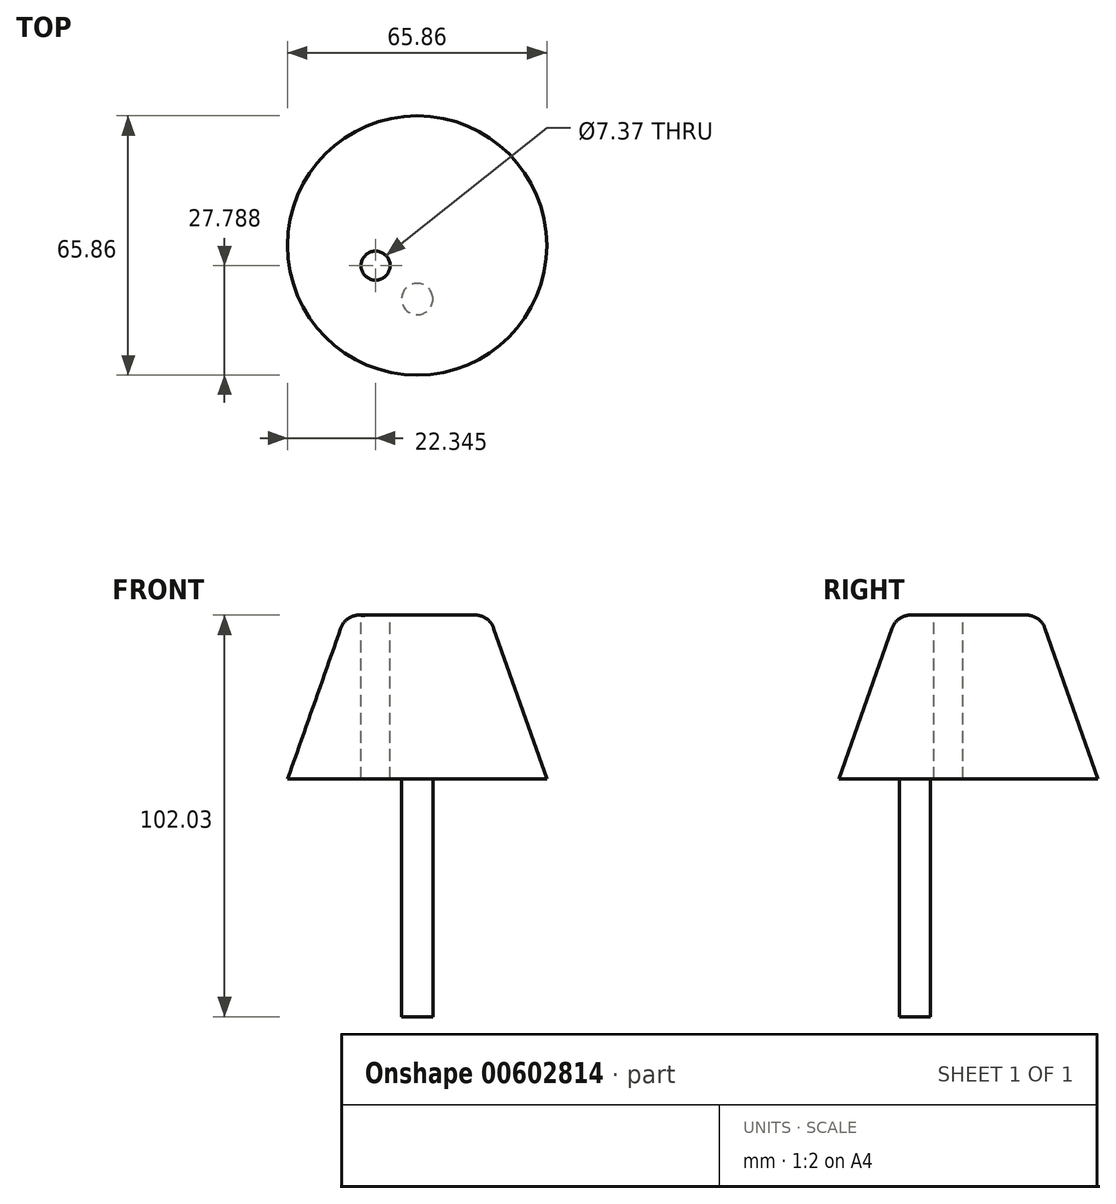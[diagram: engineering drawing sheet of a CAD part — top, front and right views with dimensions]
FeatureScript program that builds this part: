
annotation { "Feature Type Name" : "Feature", "Feature Type Description" : "" }
export const myFeature = defineFeature(function(context is Context, id is Id, definition is map)
    precondition{}
    {
        {
            var Q0;
            Q0=qCreatedBy(makeId("Front.planeOp"),FACE);
            var sketch = newSketch(context, id + "F0", { "sketchPlane" : qUnion([Q0])});
            skLineSegment(sketch, "E0", {"start": v(0, 41.64) * mm, "end": v(18.25, 41.64) * mm});
            skLineSegment(sketch, "E1", {"start": v(18.25, 41.64) * mm, "end": v(32.93, 0) * mm});
            skLineSegment(sketch, "E2", {"start": v(32.93, 0) * mm, "end": v(0, 0) * mm});
            skLineSegment(sketch, "E3", {"start": v(0, 0) * mm, "end": v(0, 41.64) * mm});
            skSolve(sketch);
        }
        {
            var Q0;
            Q0=makeQuery(id+"F0.imprint","IMPRINT",FACE,{"disambiguationData":[TD([[makeQuery(id+"F0.imprint","IMPRINT",EDGE,{"derivedFrom":sQuery(id+"F0.wireOp",EDGE,"E0")}),-1.0]])]});
            var Q1;
            Q1=sQuery(id+"F0.wireOp",EDGE,"E3");
            revolve(context, id + "F1", {"entities" : qUnion([Q0]), "axis" : qUnion([Q1]), "revolveType" : RevolveType.FULL});
        }
        {
            var Q0;
            Q0=makeQuery(id+"F1.opRevolve","SWEPT_FACE",FACE,{"disambiguationData":[OSD([sQuery(id+"F0.wireOp",EDGE,"E0")])]});
            var sketch = newSketch(context, id + "F2", { "sketchPlane" : qUnion([Q0])});
            skCircle(sketch, "E4", {"center": v(-10.59, -5.14) * mm, "radius": 3.69 * mm});
            skSolve(sketch);
        }
        {
            var Q0;
            Q0 = qSketchRegion(id + "F2", true);
            extrude(context, id + "F3", {"entities" : qUnion([Q0]), "operationType" : NewBodyOperationType.REMOVE, "endBound" : BoundingType.THROUGH_ALL, "oppositeDirection" : true, "depth" : 25 * mm, "offsetDistance" : 25 * mm});
        }
        {
            var Q0;
            Q0=makeQuery(id+"F1.opRevolve","SWEPT_FACE",FACE,{"disambiguationData":[OSD([sQuery(id+"F0.wireOp",EDGE,"E0")])]});
            var sketch = newSketch(context, id + "F4", { "sketchPlane" : qUnion([Q0])});
            skCircle(sketch, "E5", {"center": v(0, -13.75) * mm, "radius": 3.9 * mm});
            skSolve(sketch);
        }
        {
            var Q0;
            Q0 = qSketchRegion(id + "F4", true);
            extrude(context, id + "F5", {"entities" : qUnion([Q0]), "operationType" : NewBodyOperationType.ADD, "oppositeDirection" : true, "depth" : 25 * mm, "offsetDistance" : 25 * mm});
        }
        {
            var Q0;
            Q0=makeQuery(id+"F1.opRevolve","SWEPT_FACE",FACE,{"disambiguationData":[OSD([sQuery(id+"F0.wireOp",EDGE,"E0")])]});
            var sketch = newSketch(context, id + "F6", { "sketchPlane" : qUnion([Q0])});
            skCircle(sketch, "E6", {"center": v(0, -13.63) * mm, "radius": 3.98 * mm});
            skSolve(sketch);
        }
        {
            var Q0;
            Q0 = qSketchRegion(id + "F6", true);
            extrude(context, id + "F7", {"entities" : qUnion([Q0]), "operationType" : NewBodyOperationType.ADD, "endBound" : BoundingType.THROUGH_ALL, "oppositeDirection" : true, "depth" : 25 * mm, "offsetDistance" : 25 * mm});
        }
        {
            var Q0;
            Q0=makeQuery(id+"F1.opRevolve","SWEPT_FACE",FACE,{"disambiguationData":[OSD([sQuery(id+"F0.wireOp",EDGE,"E0")])]});
            var sketch = newSketch(context, id + "F8", { "sketchPlane" : qUnion([Q0])});
            skSolve(sketch);
        }
        {
            var Q0;
            Q0=makeQuery(id+"F1.opRevolve","SWEPT_EDGE",EDGE,{"disambiguationData":[OSD([sQuery(id+"F0.wireOp",EDGE,"E0"),sQuery(id+"F0.wireOp",EDGE,"E1")])]});
            fillet(context, id + "F9", {"entities" : qUnion([Q0]), "radius" : 5 * mm, "tangentPropagation" : true, "allowEdgeOverflow" : false});
        }
    });
